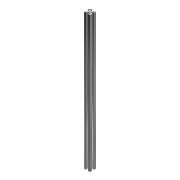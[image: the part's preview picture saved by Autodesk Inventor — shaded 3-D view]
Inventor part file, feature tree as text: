
AUTODESK INVENTOR PART (.ipt)
format: ipt  version: 2018 (Build 220112000, 112)  size: 148,992 bytes
history: native  units: mm
features: extrude x1, sketch x1
ambient origin geometry x8: Origin, YZ Plane, XZ Plane, XY Plane, X Axis, Y Axis, Z Axis, Center Point
bodies: Solid1 (feature_tree)
feature tree (2):
  extrude  "Extrusion1"  [1 undecoded]
  sketch  "Sketch1"  dims[d0=450.0mm d1=0.0mm]
note: 1 required parameter value undecoded (feature->parameter linkage not recoverable at this tier; creation-order binding heuristic only, values carry confidence <= 0.55)
